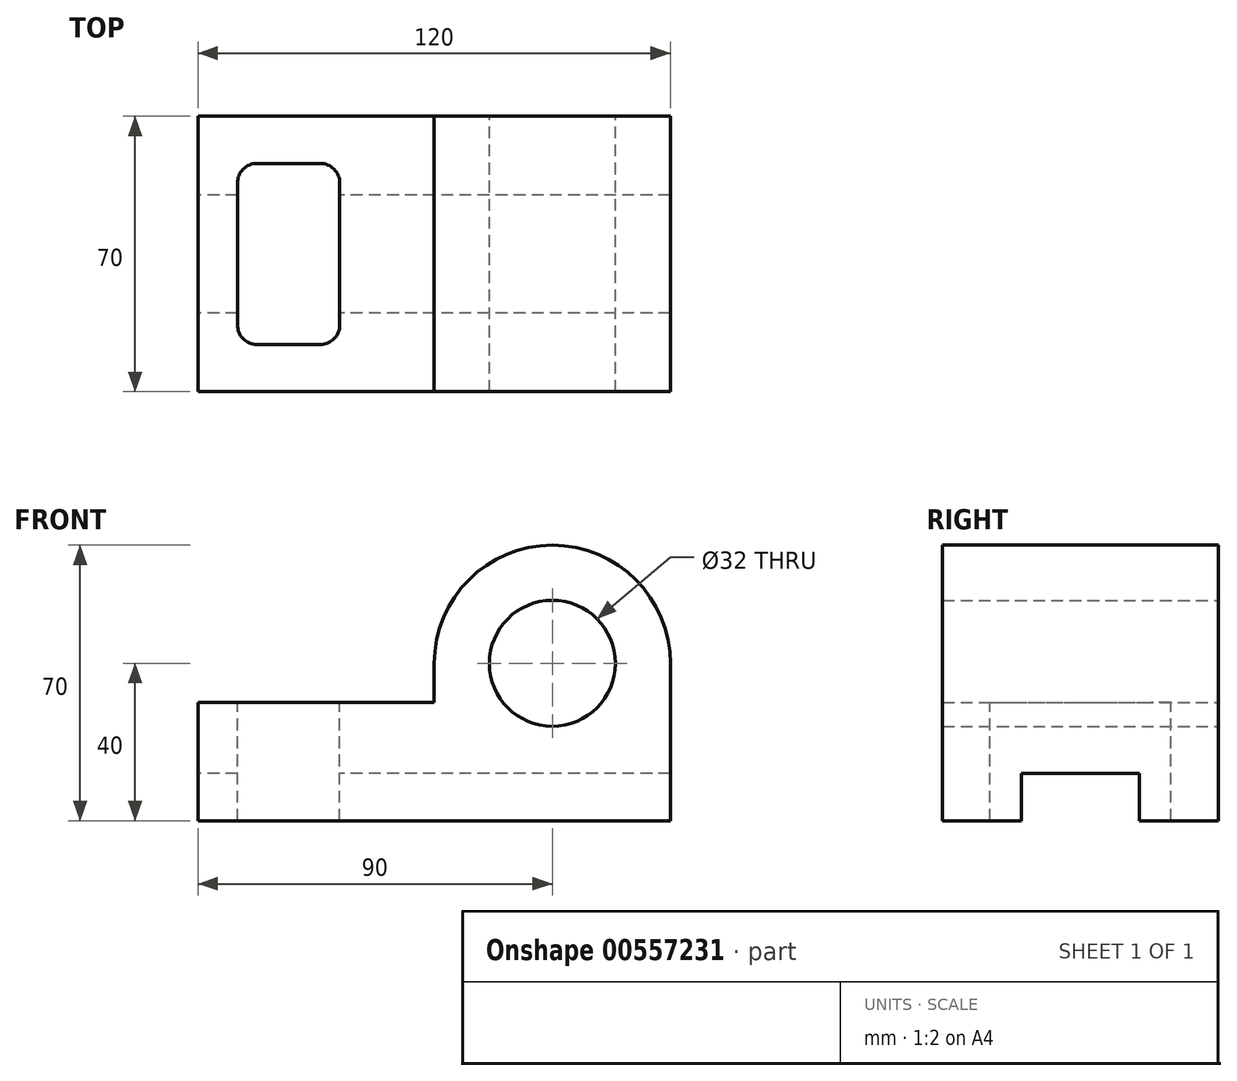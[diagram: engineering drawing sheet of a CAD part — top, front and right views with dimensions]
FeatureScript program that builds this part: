
annotation { "Feature Type Name" : "Feature", "Feature Type Description" : "" }
export const myFeature = defineFeature(function(context is Context, id is Id, definition is map)
    precondition{}
    {
        {
            var Q0;
            Q0=qCreatedBy(makeId("Front.planeOp"),FACE);
            var sketch = newSketch(context, id + "F0", { "sketchPlane" : qUnion([Q0])});
            skLineSegment(sketch, "E0.bottom", {"start": v(60, -35) * mm, "end": v(-60, -35) * mm});
            skLineSegment(sketch, "E0.left", {"start": v(60, -35) * mm, "end": v(60, 5) * mm});
            skLineSegment(sketch, "E0.right", {"start": v(-60, -35) * mm, "end": v(-60, -5) * mm});
            skPoint(sketch, "E0.middle", {"position": v(0, 0) * mm});
            skLineSegment(sketch, "E1", {"start": v(-60, -5) * mm, "end": v(0, -5) * mm});
            skLineSegment(sketch, "E2", {"start": v(0, -5) * mm, "end": v(0, 5) * mm});
            skArc(sketch, "E3", {"start": v(60, 5) * mm, "mid": v(30, 35) * mm, "end": v(0, 5) * mm});
            skPoint(sketch, "E3.second.point", {"position": v(60, 5) * mm});
            skPoint(sketch, "E3.third.point", {"position": v(30, 35) * mm});
            skPoint(sketch, "E4.orphan", {"position": v(-60, 35) * mm});
            skPoint(sketch, "E5.orphan", {"position": v(60, 35) * mm});
            skCircle(sketch, "E6", {"center": v(30, 5) * mm, "radius": 16 * mm});
            skSolve(sketch);
        }
        {
            var Q0;
            Q0 = qSketchRegion(id + "F0", true);
            extrude(context, id + "F1", {"entities" : qUnion([Q0]), "depth" : 70 * mm, "offsetDistance" : 25 * mm});
        }
        {
            var Q0;
            Q0=makeQuery(id+"F1.opExtrude","SWEPT_FACE",FACE,{"disambiguationData":[OSD([sQuery(id+"F0.wireOp",EDGE,"E1")])]});
            var sketch = newSketch(context, id + "F2", { "sketchPlane" : qUnion([Q0])});
            skLineSegment(sketch, "E7.bottom", {"start": v(-29, -58) * mm, "end": v(-45, -58) * mm});
            skLineSegment(sketch, "E7.top", {"start": v(-29, -12) * mm, "end": v(-45, -12) * mm});
            skLineSegment(sketch, "E7.left", {"start": v(-24, -53) * mm, "end": v(-24, -17) * mm});
            skLineSegment(sketch, "E7.right", {"start": v(-50, -53) * mm, "end": v(-50, -17) * mm});
            skPoint(sketch, "E7.middle", {"position": v(-37, -35) * mm});
            skPoint(sketch, "E8", {"position": v(-60, -35) * mm});
            skPoint(sketch, "E9.visualSharp", {"position": v(-24, -12) * mm});
            skArc(sketch, "E9.filletArc", {"start": v(-24, -17) * mm, "mid": v(-25.46, -13.46) * mm, "end": v(-29, -12) * mm});
            skPoint(sketch, "E10.visualSharp", {"position": v(-50, -12) * mm});
            skArc(sketch, "E10.filletArc", {"start": v(-45, -12) * mm, "mid": v(-48.54, -13.46) * mm, "end": v(-50, -17) * mm});
            skPoint(sketch, "E11.visualSharp", {"position": v(-24, -58) * mm});
            skArc(sketch, "E11.filletArc", {"start": v(-29, -58) * mm, "mid": v(-25.46, -56.54) * mm, "end": v(-24, -53) * mm});
            skPoint(sketch, "E12.visualSharp", {"position": v(-50, -58) * mm});
            skArc(sketch, "E12.filletArc", {"start": v(-50, -53) * mm, "mid": v(-48.54, -56.54) * mm, "end": v(-45, -58) * mm});
            skSolve(sketch);
        }
        {
            var Q0;
            Q0 = qSketchRegion(id + "F2", true);
            extrude(context, id + "F3", {"entities" : qUnion([Q0]), "operationType" : NewBodyOperationType.REMOVE, "endBound" : BoundingType.THROUGH_ALL, "oppositeDirection" : true, "depth" : 25 * mm, "offsetDistance" : 25 * mm});
        }
        {
            var Q0;
            Q0=makeQuery(id+"F1.opExtrude","SWEPT_FACE",FACE,{"disambiguationData":[OSD([sQuery(id+"F0.wireOp",EDGE,"E0.right")])]});
            var sketch = newSketch(context, id + "F4", { "sketchPlane" : qUnion([Q0])});
            skLineSegment(sketch, "E13.bottom", {"start": v(50, -23) * mm, "end": v(20, -23) * mm});
            skLineSegment(sketch, "E13.top", {"start": v(50, -35) * mm, "end": v(20, -35) * mm});
            skLineSegment(sketch, "E13.left", {"start": v(50, -23) * mm, "end": v(50, -35) * mm});
            skLineSegment(sketch, "E13.right", {"start": v(20, -23) * mm, "end": v(20, -35) * mm});
            skPoint(sketch, "E13.middle", {"position": v(35, -29) * mm});
            skPoint(sketch, "E14", {"position": v(35, -35) * mm});
            skSolve(sketch);
        }
        {
            var Q0;
            Q0 = qSketchRegion(id + "F4", true);
            extrude(context, id + "F5", {"entities" : qUnion([Q0]), "operationType" : NewBodyOperationType.REMOVE, "endBound" : BoundingType.THROUGH_ALL, "oppositeDirection" : true, "depth" : 25 * mm, "offsetDistance" : 25 * mm});
        }
    });
